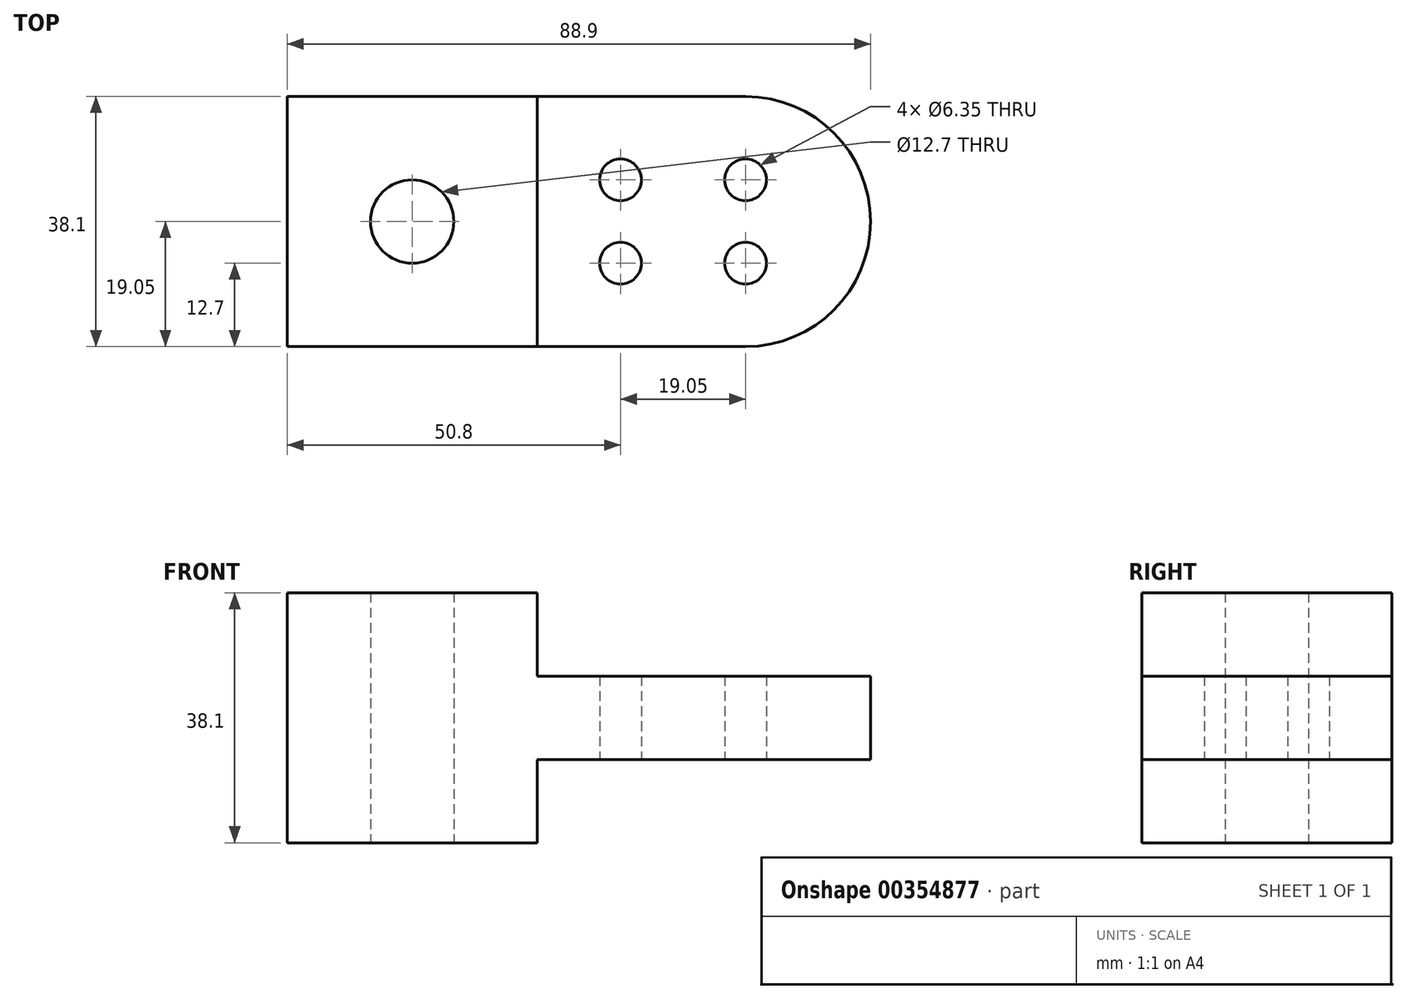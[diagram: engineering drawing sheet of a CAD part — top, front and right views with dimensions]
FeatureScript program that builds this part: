
annotation { "Feature Type Name" : "Feature", "Feature Type Description" : "" }
export const myFeature = defineFeature(function(context is Context, id is Id, definition is map)
    precondition{}
    {
        {
            var Q0;
            Q0=qCreatedBy(makeId("Top.planeOp"),FACE);
            var sketch = newSketch(context, id + "F0", { "sketchPlane" : qUnion([Q0])});
            skLineSegment(sketch, "E0", {"start": v(0, 0) * mm, "end": v(0, 38.1) * mm});
            skLineSegment(sketch, "E1", {"start": v(0, 38.1) * mm, "end": v(31.75, 38.1) * mm});
            skLineSegment(sketch, "E2", {"start": v(0, 0) * mm, "end": v(31.75, 0) * mm});
            skArc(sketch, "E3", {"start": v(31.75, 0) * mm, "mid": v(50.8, 19.05) * mm, "end": v(31.75, 38.1) * mm});
            skCircle(sketch, "E4", {"center": v(12.7, 25.4) * mm, "radius": 3.18 * mm});
            skCircle(sketch, "E5", {"center": v(12.7, 12.7) * mm, "radius": 3.18 * mm});
            skCircle(sketch, "E6", {"center": v(31.75, 12.7) * mm, "radius": 3.18 * mm});
            skCircle(sketch, "E7", {"center": v(31.75, 25.4) * mm, "radius": 3.18 * mm});
            skSolve(sketch);
        }
        {
            var Q0;
            Q0 = qSketchRegion(id + "F0", true);
            extrude(context, id + "F1", {"entities" : qUnion([Q0]), "depth" : 12.7 * mm});
        }
        {
            var Q0;
            Q0=qCreatedBy(makeId("Top.planeOp"),FACE);
            var sketch = newSketch(context, id + "F2", { "sketchPlane" : qUnion([Q0])});
            skLineSegment(sketch, "E8.bottom", {"start": v(0, 0) * mm, "end": v(-38.1, 0) * mm});
            skLineSegment(sketch, "E8.top", {"start": v(0, 38.1) * mm, "end": v(-38.1, 38.1) * mm});
            skLineSegment(sketch, "E8.left", {"start": v(0, 0) * mm, "end": v(0, 38.1) * mm});
            skLineSegment(sketch, "E8.right", {"start": v(-38.1, 0) * mm, "end": v(-38.1, 38.1) * mm});
            skCircle(sketch, "E9", {"center": v(-19.05, 19.05) * mm, "radius": 6.35 * mm});
            skPoint(sketch, "E9.centerSnap0", {"position": v(-19.05, 38.1) * mm});
            skPoint(sketch, "E9.centerSnap1", {"position": v(0, 19.05) * mm});
            skSolve(sketch);
        }
        {
            var Q0;
            Q0 = qSketchRegion(id + "F2", true);
            extrude(context, id + "F3", {"entities" : qUnion([Q0]), "operationType" : NewBodyOperationType.ADD, "depth" : 25.4 * mm, "hasSecondDirection" : true, "secondDirectionOppositeDirection" : true, "secondDirectionDepth" : 12.7 * mm});
        }
    });
